# Revit family: Haworth_Riverbend_ConcaveCurve90_EU_PRELIMINARY
name_source: partatom
category: Furniture
revit_build: Autodesk Revit 2018 (Build: 20170223_1515(x64)
units: mm (PartAtom-declared; Revit-internal decimal feet)

## family parameters
Always vertical = Yes
Cut with Voids When Loaded = No
OmniClass Number = 23.40.70.14.64.21
OmniClass Title = Systems Furniture
Room Calculation Point = No
Shared = No
Work Plane-Based = No

## types (6) — shared parameters
Actual Height = 45 cm
Actual Width = 143 cm
Arms = Not available for No Back
Assembly Code = E2020200
Description = Haworth - Riverbend - Concave Curve - 90 Degree
Manufacturer = Haworth
Model = SELSCX90
Revision Number = 1
Size = Verify Final Dim. w/ Haworth
Trim Finish = Haworth _ Paint _ Plaster
URL = https://www.haworth.com
URL - Product = https://www.haworth.com
Warranty = http://www.haworth.com

## per-type parameters (varying)
| type | Actual Depth | High Back | Large | Mid Back | No Back | Small | Width Straight Edge |
| 45 x 90 x 143 - No Back | 85 cm | No | Yes | No | Yes | No | 85 cm |
| 78 x 90 x 143 - Mid Back | 85 cm | No | Yes | Yes | No | No | 85 cm |
| 126 x 90 x 143 - High Back | 85 cm | Yes | Yes | No | No | No | 85 cm |
| 126 x 84 x 143 - High Back | 79 cm | Yes | No | No | No | Yes | 79 cm |
| 45 x 84 x 143 - No Back | 79 cm | No | No | No | Yes | Yes | 79 cm |
| 78 x 84 x 143 - Mid Back | 79 cm | No | No | Yes | No | Yes | 79 cm |

## geometry (parser evidence)
native form markers: Sweep x16
no freeform markers — native parametric forms only
